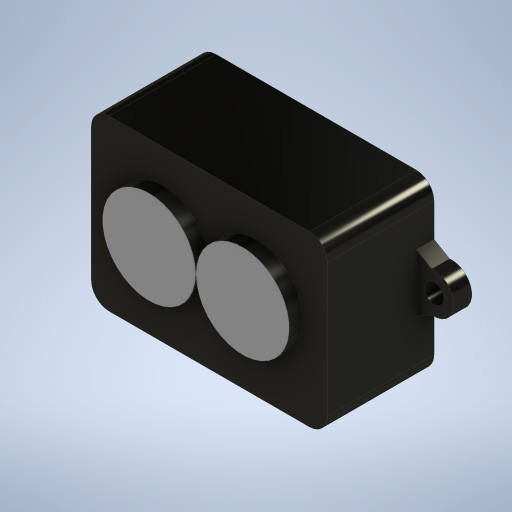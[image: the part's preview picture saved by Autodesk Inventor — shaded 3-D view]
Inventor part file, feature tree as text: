
AUTODESK INVENTOR PART (.ipt)
format: ipt  version: 2023.1 (Build 271208000, 208)  size: 331,776 bytes
history: native  units: in
note: dims shown in document units (in); Inventor stores cm internally (conversion verified against a paired STEP export)
features: extrude x5, sketch x2, fillet x1
ambient origin geometry x8: Origin, YZ Plane, XZ Plane, XY Plane, X Axis, Y Axis, Z Axis, Center Point
bodies: Solid1 (feature_tree)
feature tree (8):
  sketch  "Sketch1"  dims[d0=1.0433in d1=0.748in]
  extrude  "Extrusion1"  Depth=0.748in
  extrude  "Extrusion2"  Depth=0.8366in
  extrude  "Extrusion3"  Depth=0.7087in
  fillet  "Fillet1"  Radius=0.0866in
  extrude  "Extrusion4"  Depth=0.5315in
  extrude  "Extrusion5"  Depth=0.5315in
  sketch  "Sketch2"  dims[d2=0.0787in d3=0.8366in d4=0.7087in d5=0.0866in d6=0.1772in d7=0.1772in d8=0.3543in d9=1.2008in d10=0.4134in d11=0.4134in d12=0.4134in d13=0.6004in d14=60.0deg d15=60.0deg d16=0.128in d17=0.128in d18=0.3937in d19=0.3937in d20=60.0deg d21=60.0deg d22=0.128in d23=0.128in d24=0.3937in d25=0.3937in d26=0.4724in d27=0.0in d28=0.0787in d29=0.0in d30=0.315in d31=0.0in d32=0.0394in d33=0.2677in d35=0.4134in d36=0.0394in d37=0.0394in d38=0.0in d39=0.5315in d40=0.0in]
